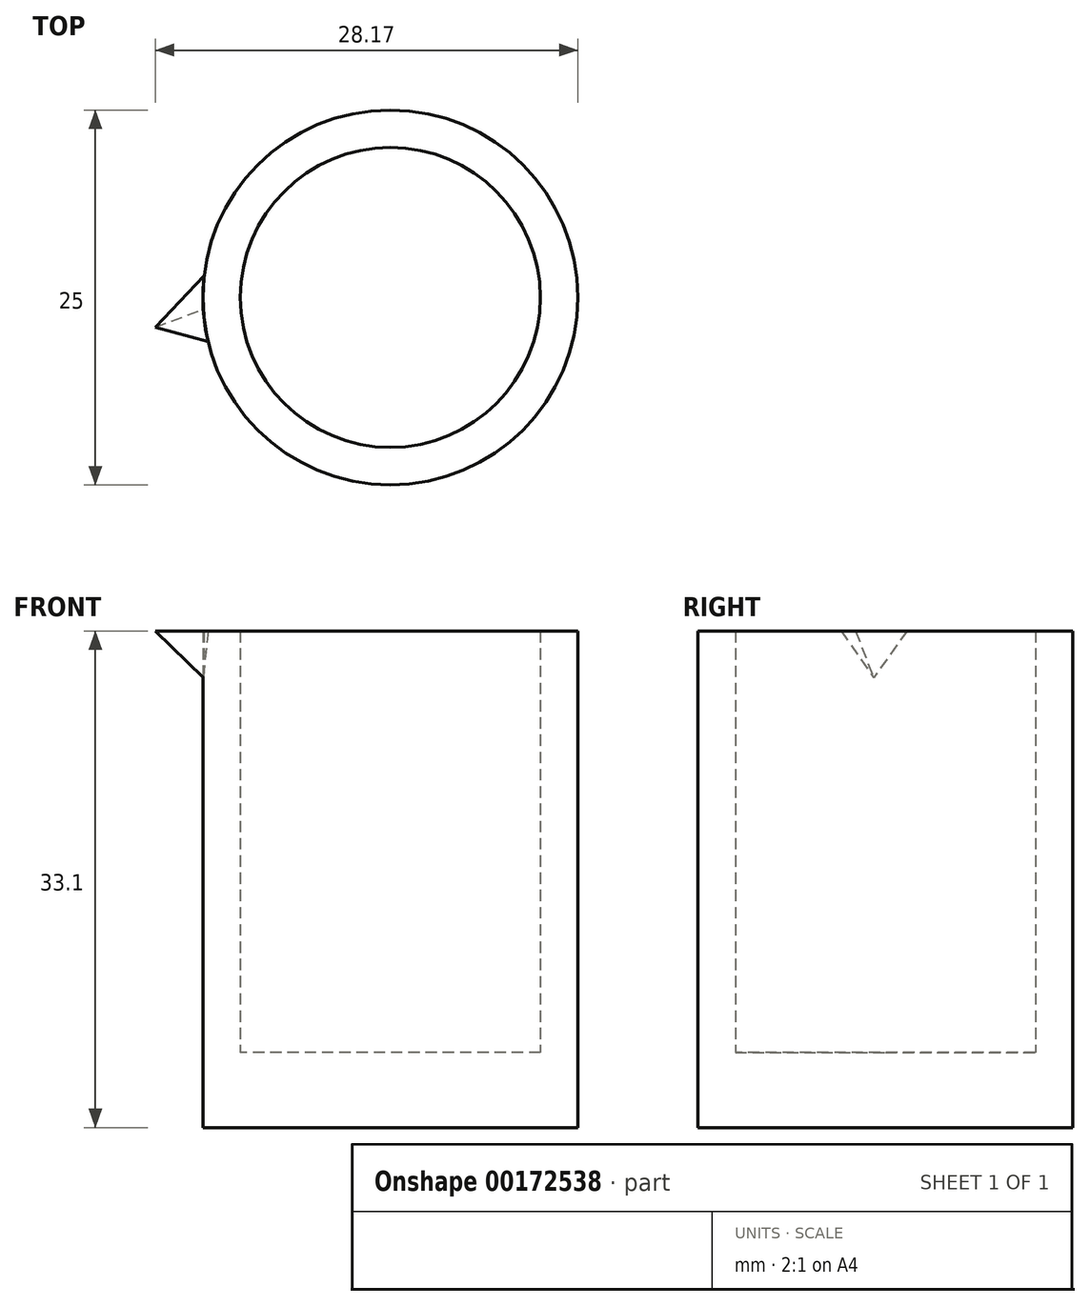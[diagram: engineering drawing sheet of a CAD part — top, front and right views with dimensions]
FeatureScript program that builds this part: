
annotation { "Feature Type Name" : "Feature", "Feature Type Description" : "" }
export const myFeature = defineFeature(function(context is Context, id is Id, definition is map)
    precondition{}
    {
        {
            var Q0;
            Q0=qCreatedBy(makeId("Top.planeOp"),FACE);
            var sketch = newSketch(context, id + "F0", { "sketchPlane" : qUnion([Q0])});
            skCircle(sketch, "E0", {"center": v(0, 0) * mm, "radius": 12.5 * mm});
            skCircle(sketch, "E1", {"center": v(0, 0) * mm, "radius": 10 * mm});
            skPoint(sketch, "E2.start.orphan", {"position": v(-14.35, 0) * mm});
            skSolve(sketch);
        }
        {
            var Q0;
            Q0=makeQuery(id+"F0.imprint","IMPRINT",FACE,{"disambiguationData":[TD([[makeQuery(id+"F0.imprint","IMPRINT",EDGE,{"derivedFrom":sQuery(id+"F0.wireOp",EDGE,"E0")}),1.0]])]});
            var Q1;
            {var subQ0=sQuery(id+"F0.wireOp",EDGE,"wONsm84D-ABhV-dbH5-FFea-0SnDX2Vs03So");Q1=makeQuery(id+"F0.imprint","IMPRINT",FACE,{"disambiguationData":[TD([[makeQuery(id+"F0.imprint","IMPRINT",EDGE,{"derivedFrom":subQ0}),1.0]])]});}
            extrude(context, id + "F1", {"entities" : qUnion([Q0, Q1]), "depth" : 28.1 * mm});
        }
        {
            var Q0;
            Q0=qCreatedBy(makeId("Top.planeOp"),FACE);
            var sketch = newSketch(context, id + "F2", { "sketchPlane" : qUnion([Q0])});
            skCircle(sketch, "E3", {"center": v(0, 0) * mm, "radius": 12.5 * mm});
            skSolve(sketch);
        }
        {
            var Q0;
            Q0 = qSketchRegion(id + "F2", true);
            var Q1;
            Q1=makeQuery(id+"F1.opExtrude","CAP_FACE",FACE,{"disambiguationData":[OSD([sQuery(id+"F0.wireOp",EDGE,"E0"),sQuery(id+"F0.wireOp",EDGE,"E1")])],"isStart":false});
            extrude(context, id + "F3", {"entities" : qUnion([Q0, Q1]), "operationType" : NewBodyOperationType.ADD, "depth" : 5 * mm});
        }
        {
            var Q0;
            Q0=makeQuery(id+"F3.opExtrude","CAP_FACE",FACE,{"disambiguationData":[OSD([sQuery(id+"F0.wireOp",EDGE,"E0"),sQuery(id+"F0.wireOp",EDGE,"E1")])],"isStart":false});
            var sketch = newSketch(context, id + "F4", { "sketchPlane" : qUnion([Q0])});
            skLineSegment(sketch, "E4", {"start": v(-12.42, 1.45) * mm, "end": v(-15.67, -1.97) * mm});
            skLineSegment(sketch, "E5", {"start": v(-15.67, -1.97) * mm, "end": v(-12.15, -2.95) * mm});
            skSolve(sketch);
        }
        {
            var Q0;
            Q0=qCreatedBy(makeId("Top.planeOp"),FACE);
            cPlane(context, id + "F5", {"entities" : qUnion([Q0]), "cplaneType" : CPlaneType.OFFSET, "offset" : 30 * mm, "width" : 150 * mm, "height" : 150 * mm});
        }
        {
            var Q0;
            Q0=qCreatedBy(id+"F5.planeOp",FACE);
            var sketch = newSketch(context, id + "F6", { "sketchPlane" : qUnion([Q0])});
            skPoint(sketch, "E6", {"position": v(-12.47, -0.78) * mm});
            skSolve(sketch);
        }
        {
            var Q0;
            {var subQ0=sQuery(id+"F4.wireOp",EDGE,"E4");Q0=makeQuery(id+"F4.imprint","IMPRINT",FACE,{"disambiguationData":[TD([[makeQuery(id+"F4.imprint","IMPRINT",EDGE,{"derivedFrom":subQ0}),1.0]])]});}
            var Q1;
            Q1=sQuery(id+"F6.wireOp",VERTEX,"E6");
            loft(context, id + "F7", {"sheetProfilesArray" : [{ "sheetProfileEntities" : qUnion([Q0]) }, { "sheetProfileEntities" : qUnion([Q1]) }]});
        }
    });
